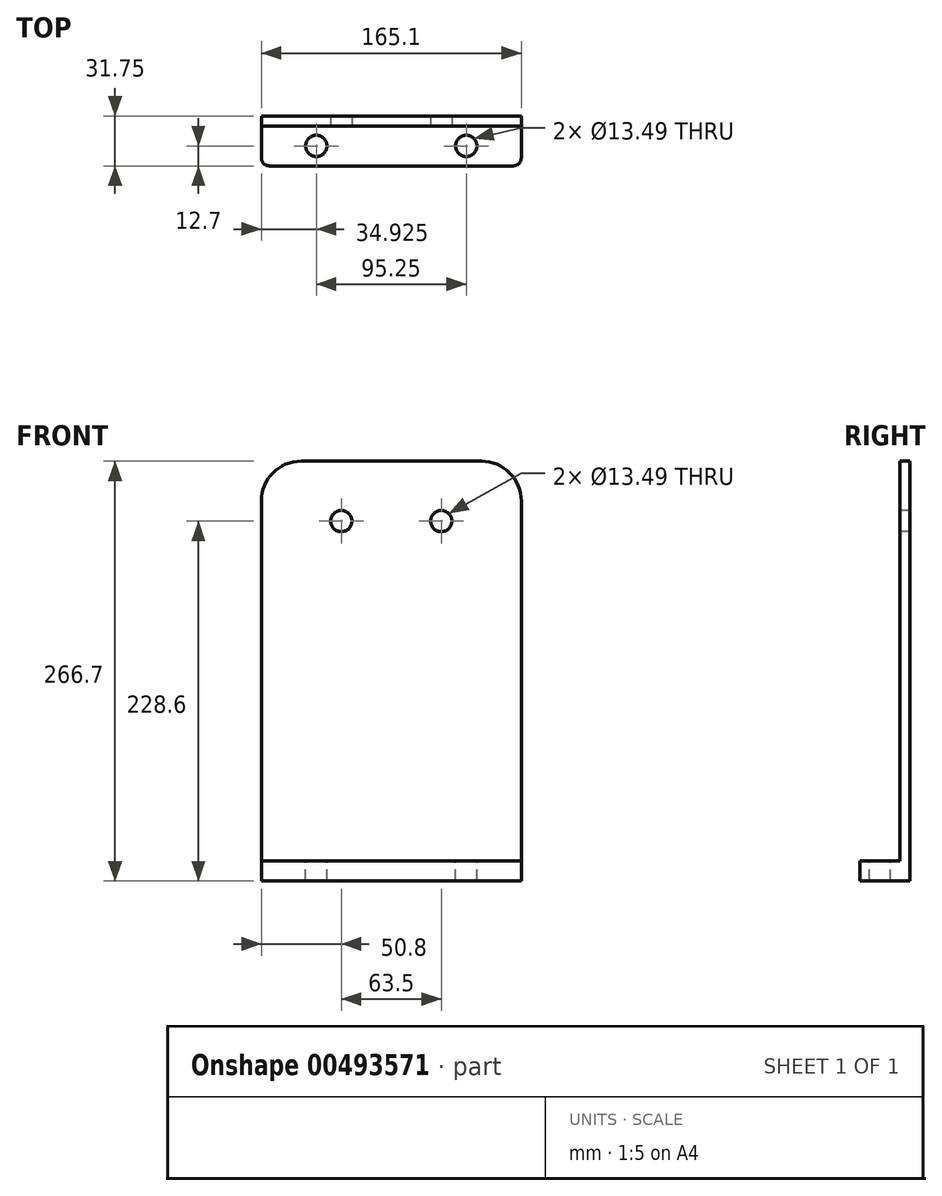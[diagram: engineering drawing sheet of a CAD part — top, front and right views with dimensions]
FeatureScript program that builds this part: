
annotation { "Feature Type Name" : "Feature", "Feature Type Description" : "" }
export const myFeature = defineFeature(function(context is Context, id is Id, definition is map)
    precondition{}
    {
        {
            var Q0;
            Q0=qCreatedBy(makeId("Front.planeOp"),FACE);
            var sketch = newSketch(context, id + "F0", { "sketchPlane" : qUnion([Q0])});
            skLineSegment(sketch, "E0.bottom", {"start": v(0, 0) * mm, "end": v(165.1, 0) * mm});
            skLineSegment(sketch, "E0.top", {"start": v(25.4, 266.7) * mm, "end": v(139.7, 266.7) * mm});
            skLineSegment(sketch, "E0.left", {"start": v(0, 0) * mm, "end": v(0, 241.3) * mm});
            skLineSegment(sketch, "E0.right", {"start": v(165.1, 0) * mm, "end": v(165.1, 241.3) * mm});
            skPoint(sketch, "E1.visualSharp", {"position": v(0, 266.7) * mm});
            skArc(sketch, "E1.filletArc", {"start": v(25.4, 266.7) * mm, "mid": v(7.44, 259.26) * mm, "end": v(0, 241.3) * mm});
            skPoint(sketch, "E2.visualSharp", {"position": v(165.1, 266.7) * mm});
            skArc(sketch, "E2.filletArc", {"start": v(165.1, 241.3) * mm, "mid": v(157.66, 259.26) * mm, "end": v(139.7, 266.7) * mm});
            skSolve(sketch);
        }
        {
            var Q0;
            Q0 = qSketchRegion(id + "F0", true);
            extrude(context, id + "F1", {"entities" : qUnion([Q0]), "depth" : 6.35 * mm});
        }
        {
            var Q0;
            Q0=makeQuery(id+"F1.opExtrude","CAP_FACE",FACE,{"disambiguationData":[OSD([sQuery(id+"F0.wireOp",EDGE,"E0.bottom"),sQuery(id+"F0.wireOp",EDGE,"E0.top"),sQuery(id+"F0.wireOp",EDGE,"E0.left"),sQuery(id+"F0.wireOp",EDGE,"E0.right"),sQuery(id+"F0.wireOp",EDGE,"E1.filletArc"),sQuery(id+"F0.wireOp",EDGE,"E2.filletArc")])],"isStart":false});
            var sketch = newSketch(context, id + "F2", { "sketchPlane" : qUnion([Q0])});
            skPoint(sketch, "E3", {"position": v(50.8, 228.6) * mm});
            skPoint(sketch, "E4", {"position": v(114.3, 228.6) * mm});
            skSolve(sketch);
        }
        {
            var Q0;
            Q0=sQuery(id+"F2.wireOp",VERTEX,"E3");
            var Q1;
            Q1=sQuery(id+"F2.wireOp",VERTEX,"E4");
            var Q2;
            Q2=makeQuery(id+"F1.opExtrude","SWEPT_BODY",BODY,{"disambiguationData":[OSD([sQuery(id+"F0.wireOp",EDGE,"E0.bottom"),sQuery(id+"F0.wireOp",EDGE,"E0.top"),sQuery(id+"F0.wireOp",EDGE,"E0.left"),sQuery(id+"F0.wireOp",EDGE,"E0.right"),sQuery(id+"F0.wireOp",EDGE,"E1.filletArc"),sQuery(id+"F0.wireOp",EDGE,"E2.filletArc")])]});
            hole(context, id + "F3", {"style" : HoleStyle.SIMPLE, "endStyle" : HoleEndStyle.THROUGH, "standardTappedOrClearance" : lookupTablePath({ "standard" : "ANSI", "fit" : "Normal (ASME)", "size" : "1/2", "type" : "Clearance" }), "standardBlindInLast" : lookupTablePath({ "fit" : "Free", "standard" : "ANSI", "size" : "1/2", "type" : "Clearance" }), "holeDiameter" : 13.5 * mm, "tappedDepth" : 20.64 * mm, "tapClearance" : 3, "startFromSketch" : true, "locations" : qUnion([Q0, Q1]), "scope" : qUnion([Q2])});
        }
        {
            var Q0;
            Q0=makeQuery(id+"F1.opExtrude","CAP_FACE",FACE,{"disambiguationData":[OSD([sQuery(id+"F0.wireOp",EDGE,"E0.bottom"),sQuery(id+"F0.wireOp",EDGE,"E0.top"),sQuery(id+"F0.wireOp",EDGE,"E0.left"),sQuery(id+"F0.wireOp",EDGE,"E0.right"),sQuery(id+"F0.wireOp",EDGE,"E1.filletArc"),sQuery(id+"F0.wireOp",EDGE,"E2.filletArc")])],"isStart":false});
            var sketch = newSketch(context, id + "F4", { "sketchPlane" : qUnion([Q0])});
            skLineSegment(sketch, "E5.bottom", {"start": v(0, 0) * mm, "end": v(165.1, 0) * mm});
            skLineSegment(sketch, "E5.top", {"start": v(0, 12.7) * mm, "end": v(165.1, 12.7) * mm});
            skLineSegment(sketch, "E5.left", {"start": v(0, 0) * mm, "end": v(0, 12.7) * mm});
            skLineSegment(sketch, "E5.right", {"start": v(165.1, 0) * mm, "end": v(165.1, 12.7) * mm});
            skSolve(sketch);
        }
        {
            var Q0;
            Q0 = qSketchRegion(id + "F4", true);
            extrude(context, id + "F5", {"entities" : qUnion([Q0]), "operationType" : NewBodyOperationType.ADD, "depth" : 25.4 * mm});
        }
        {
            var Q0;
            Q0=makeQuery(id+"F5.opExtrude","CAP_EDGE",EDGE,{"disambiguationData":[OSD([sQuery(id+"F4.wireOp",EDGE,"E5.right")])],"isStart":false});
            var Q1;
            Q1=makeQuery(id+"F5.opExtrude","CAP_EDGE",EDGE,{"disambiguationData":[OSD([sQuery(id+"F4.wireOp",EDGE,"E5.left")])],"isStart":false});
            fillet(context, id + "F6", {"entities" : qUnion([Q0, Q1]), "radius" : 5.08 * mm, "tangentPropagation" : true, "allowEdgeOverflow" : false});
        }
        {
            var Q0;
            Q0=makeQuery(id+"F5.opExtrude","SWEPT_FACE",FACE,{"disambiguationData":[OSD([sQuery(id+"F4.wireOp",EDGE,"E5.top")])]});
            var sketch = newSketch(context, id + "F7", { "sketchPlane" : qUnion([Q0])});
            skPoint(sketch, "E6", {"position": v(34.92, -19.05) * mm});
            skPoint(sketch, "E7", {"position": v(130.18, -19.05) * mm});
            skSolve(sketch);
        }
        {
            var Q0;
            Q0=sQuery(id+"F7.wireOp",VERTEX,"E6");
            var Q1;
            Q1=sQuery(id+"F7.wireOp",VERTEX,"E7");
            var Q2;
            Q2=makeQuery(id+"F1.opExtrude","SWEPT_BODY",BODY,{"disambiguationData":[OSD([sQuery(id+"F0.wireOp",EDGE,"E0.bottom"),sQuery(id+"F0.wireOp",EDGE,"E0.top"),sQuery(id+"F0.wireOp",EDGE,"E0.left"),sQuery(id+"F0.wireOp",EDGE,"E0.right"),sQuery(id+"F0.wireOp",EDGE,"E1.filletArc"),sQuery(id+"F0.wireOp",EDGE,"E2.filletArc")])]});
            hole(context, id + "F8", {"style" : HoleStyle.SIMPLE, "endStyle" : HoleEndStyle.THROUGH, "standardTappedOrClearance" : lookupTablePath({ "standard" : "ANSI", "fit" : "Normal (ASME)", "size" : "1/2", "type" : "Clearance" }), "standardBlindInLast" : lookupTablePath({ "fit" : "Free", "standard" : "ANSI", "size" : "1/2", "type" : "Clearance" }), "holeDiameter" : 13.5 * mm, "tappedDepth" : 20.65 * mm, "tapClearance" : 3, "startFromSketch" : true, "locations" : qUnion([Q0, Q1]), "scope" : qUnion([Q2])});
        }
    });
